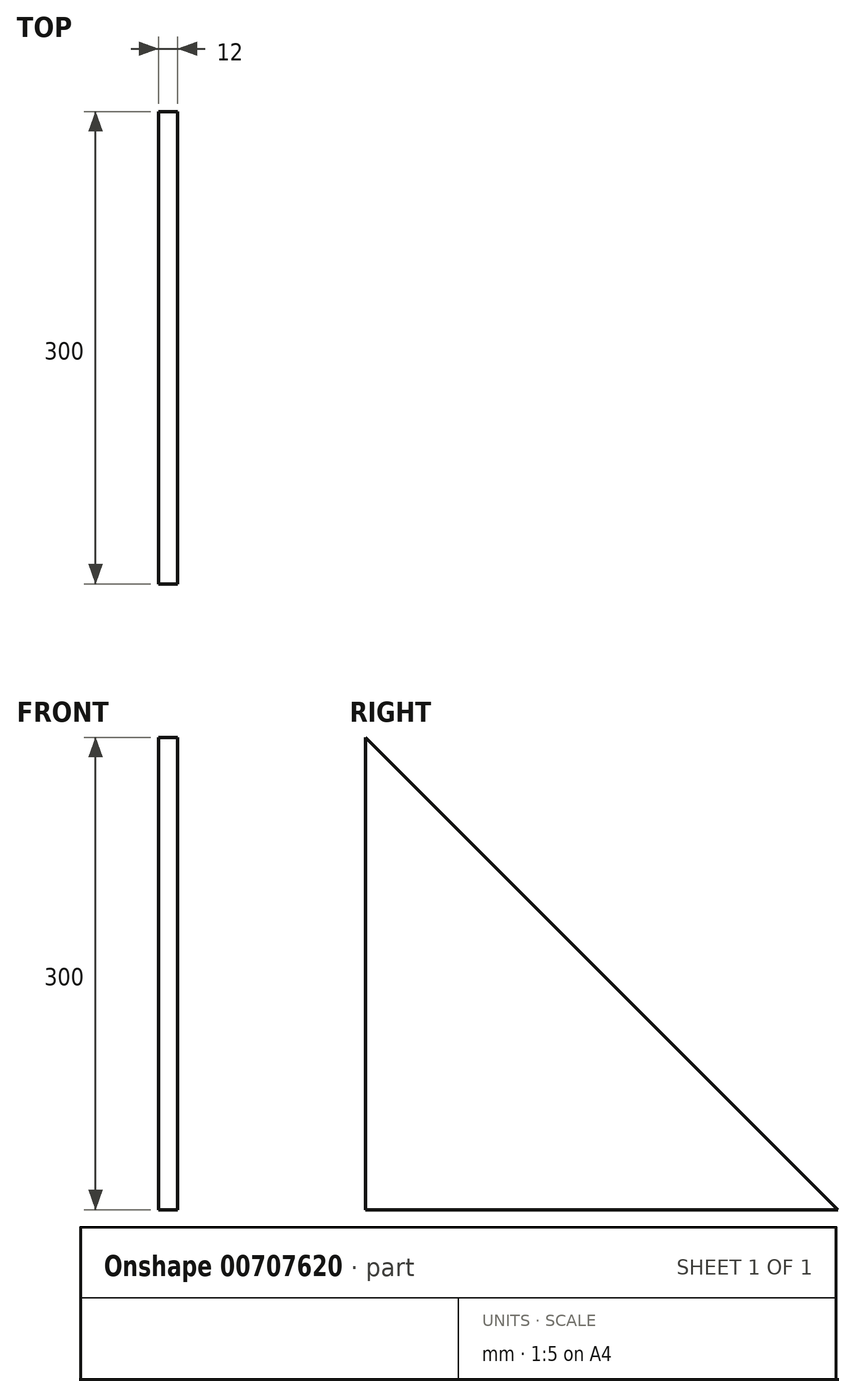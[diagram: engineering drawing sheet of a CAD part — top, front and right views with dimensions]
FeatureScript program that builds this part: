
annotation { "Feature Type Name" : "Feature", "Feature Type Description" : "" }
export const myFeature = defineFeature(function(context is Context, id is Id, definition is map)
    precondition{}
    {
        {
            var Q0;
            Q0=qCreatedBy(makeId("Right.planeOp"),FACE);
            var sketch = newSketch(context, id + "F0", { "sketchPlane" : qUnion([Q0])});
            skLineSegment(sketch, "E0", {"start": v(300, 0) * mm, "end": v(0, 0) * mm});
            skLineSegment(sketch, "E1", {"start": v(0, 0) * mm, "end": v(0, 300) * mm});
            skLineSegment(sketch, "E2", {"start": v(0, 300) * mm, "end": v(300, 0) * mm});
            skSolve(sketch);
        }
        {
            var Q0;
            Q0=makeQuery(id+"F0.imprint","IMPRINT",FACE,{"disambiguationData":[TD([[makeQuery(id+"F0.imprint","IMPRINT",EDGE,{"derivedFrom":sQuery(id+"F0.wireOp",EDGE,"E0")}),-1.0]])]});
            extrude(context, id + "F1", {"entities" : qUnion([Q0]), "depth" : 12 * mm, "offsetDistance" : 25 * mm});
        }
    });
